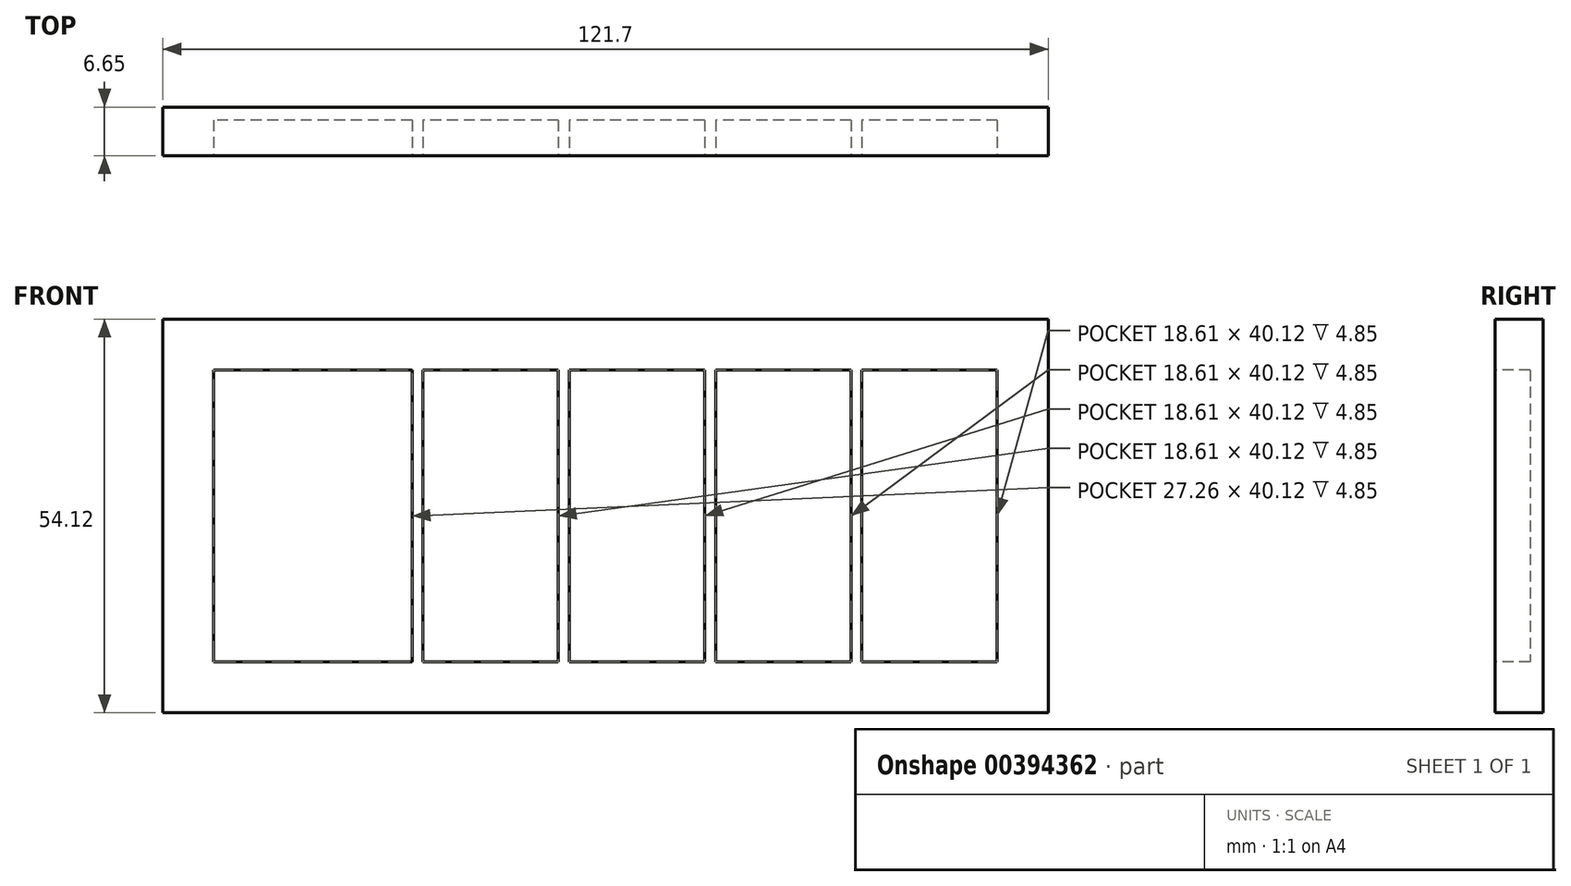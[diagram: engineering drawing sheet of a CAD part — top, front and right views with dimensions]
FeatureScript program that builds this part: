
annotation { "Feature Type Name" : "Feature", "Feature Type Description" : "" }
export const myFeature = defineFeature(function(context is Context, id is Id, definition is map)
    precondition{}
    {
        {
            var Q0;
            Q0=qCreatedBy(makeId("Front.planeOp"),FACE);
            var sketch = newSketch(context, id + "F0", { "sketchPlane" : qUnion([Q0])});
            skLineSegment(sketch, "E0.bottom", {"start": v(60.85, 27.06) * mm, "end": v(-60.85, 27.06) * mm});
            skLineSegment(sketch, "E0.top", {"start": v(60.85, -27.06) * mm, "end": v(-60.85, -27.06) * mm});
            skLineSegment(sketch, "E0.left", {"start": v(60.85, 27.06) * mm, "end": v(60.85, -27.06) * mm});
            skLineSegment(sketch, "E0.right", {"start": v(-60.85, 27.06) * mm, "end": v(-60.85, -27.06) * mm});
            skSolve(sketch);
        }
        {
            var Q0;
            Q0 = qSketchRegion(id + "F0", true);
            extrude(context, id + "F1", {"entities" : qUnion([Q0]), "depth" : 6.65 * mm});
        }
        {
            var Q0;
            Q0=makeQuery(id+"F1.opExtrude","CAP_FACE",FACE,{"disambiguationData":[OSD([sQuery(id+"F0.wireOp",EDGE,"E0.bottom"),sQuery(id+"F0.wireOp",EDGE,"E0.top"),sQuery(id+"F0.wireOp",EDGE,"E0.left"),sQuery(id+"F0.wireOp",EDGE,"E0.right")])],"isStart":false});
            var sketch = newSketch(context, id + "F2", { "sketchPlane" : qUnion([Q0])});
            skLineSegment(sketch, "E1.bottom", {"start": v(-26.59, 20.06) * mm, "end": v(-53.85, 20.06) * mm});
            skLineSegment(sketch, "E1.top", {"start": v(-26.6, -20.06) * mm, "end": v(-53.85, -20.06) * mm});
            skLineSegment(sketch, "E1.left", {"start": v(-26.59, 20.06) * mm, "end": v(-26.59, -20.06) * mm});
            skLineSegment(sketch, "E1.right", {"start": v(-53.85, 20.06) * mm, "end": v(-53.85, -20.06) * mm});
            skPoint(sketch, "E1.middle", {"position": v(-40.22, 0) * mm});
            skLineSegment(sketch, "E2.bottom", {"start": v(-6.48, 20.06) * mm, "end": v(-25.09, 20.06) * mm});
            skLineSegment(sketch, "E2.top", {"start": v(-6.48, -20.06) * mm, "end": v(-25.09, -20.06) * mm});
            skLineSegment(sketch, "E2.left", {"start": v(-6.48, 20.06) * mm, "end": v(-6.48, -20.06) * mm});
            skLineSegment(sketch, "E2.right", {"start": v(-25.09, 20.06) * mm, "end": v(-25.09, -20.06) * mm});
            skPoint(sketch, "E2.middle", {"position": v(-15.79, 0) * mm});
            skLineSegment(sketch, "E3.bottom", {"start": v(13.63, 20.06) * mm, "end": v(-4.98, 20.06) * mm});
            skLineSegment(sketch, "E3.top", {"start": v(13.63, -20.06) * mm, "end": v(-4.98, -20.06) * mm});
            skLineSegment(sketch, "E3.left", {"start": v(13.63, 20.06) * mm, "end": v(13.63, -20.06) * mm});
            skLineSegment(sketch, "E3.right", {"start": v(-4.98, 20.06) * mm, "end": v(-4.98, -20.06) * mm});
            skPoint(sketch, "E3.middle", {"position": v(4.33, 0) * mm});
            skLineSegment(sketch, "E4.bottom", {"start": v(33.74, 20.06) * mm, "end": v(15.13, 20.06) * mm});
            skLineSegment(sketch, "E4.top", {"start": v(33.74, -20.06) * mm, "end": v(15.13, -20.06) * mm});
            skLineSegment(sketch, "E4.left", {"start": v(33.74, 20.06) * mm, "end": v(33.74, -20.06) * mm});
            skLineSegment(sketch, "E4.right", {"start": v(15.13, 20.06) * mm, "end": v(15.13, -20.06) * mm});
            skPoint(sketch, "E4.middle", {"position": v(24.44, 0) * mm});
            skLineSegment(sketch, "E5.bottom", {"start": v(53.85, 20.06) * mm, "end": v(35.24, 20.06) * mm});
            skLineSegment(sketch, "E5.top", {"start": v(53.85, -20.06) * mm, "end": v(35.24, -20.06) * mm});
            skLineSegment(sketch, "E5.left", {"start": v(53.85, 20.06) * mm, "end": v(53.85, -20.06) * mm});
            skLineSegment(sketch, "E5.right", {"start": v(35.24, 20.06) * mm, "end": v(35.24, -20.06) * mm});
            skPoint(sketch, "E5.middle", {"position": v(44.55, 0) * mm});
            skSolve(sketch);
        }
        {
            var Q0;
            Q0 = qSketchRegion(id + "F2", true);
            extrude(context, id + "F3", {"entities" : qUnion([Q0]), "operationType" : NewBodyOperationType.REMOVE, "oppositeDirection" : true, "depth" : 4.85 * mm});
        }
    });
